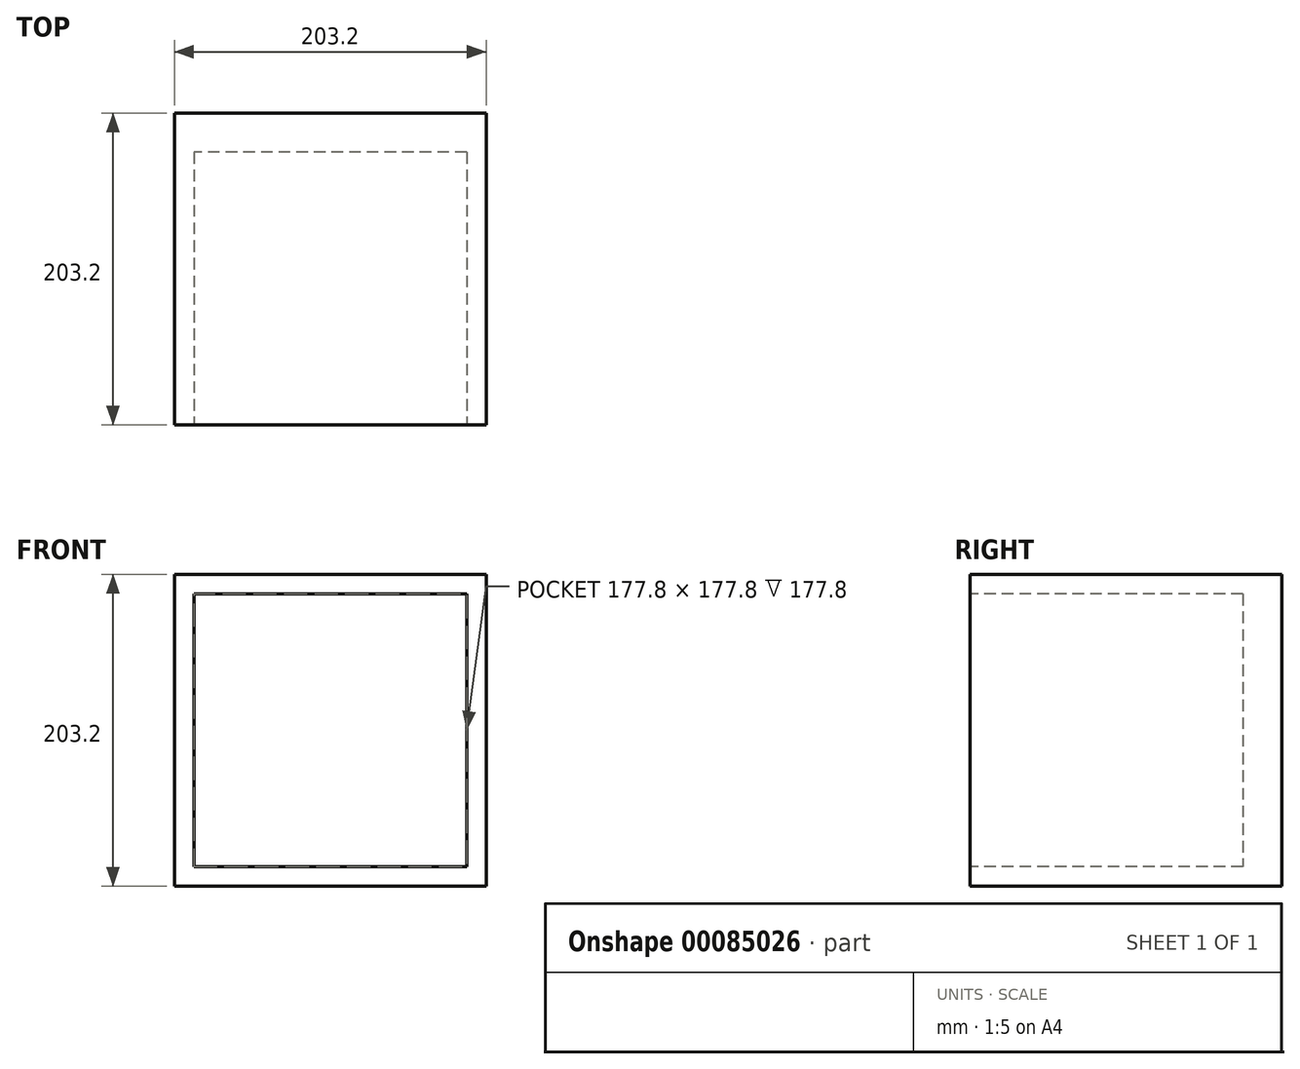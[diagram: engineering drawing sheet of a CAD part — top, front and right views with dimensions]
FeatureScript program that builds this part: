
annotation { "Feature Type Name" : "Feature", "Feature Type Description" : "" }
export const myFeature = defineFeature(function(context is Context, id is Id, definition is map)
    precondition{}
    {
        {
            var Q0;
            Q0=qCreatedBy(makeId("Front.planeOp"),FACE);
            var sketch = newSketch(context, id + "F0", { "sketchPlane" : qUnion([Q0])});
            skLineSegment(sketch, "E0.bottom", {"start": v(101.6, 101.6) * mm, "end": v(-101.6, 101.6) * mm});
            skLineSegment(sketch, "E0.top", {"start": v(101.6, -101.6) * mm, "end": v(-101.6, -101.6) * mm});
            skLineSegment(sketch, "E0.left", {"start": v(101.6, 101.6) * mm, "end": v(101.6, -101.6) * mm});
            skLineSegment(sketch, "E0.right", {"start": v(-101.6, 101.6) * mm, "end": v(-101.6, -101.6) * mm});
            skPoint(sketch, "E0.middle", {"position": v(0, 0) * mm});
            skSolve(sketch);
        }
        {
            var Q0;
            Q0 = qSketchRegion(id + "F0", true);
            extrude(context, id + "F1", {"entities" : qUnion([Q0]), "depth" : 203.2 * mm});
        }
        {
            var Q0;
            Q0=makeQuery(id+"F1.opExtrude","CAP_FACE",FACE,{"disambiguationData":[OSD([sQuery(id+"F0.wireOp",EDGE,"E0.bottom"),sQuery(id+"F0.wireOp",EDGE,"E0.top"),sQuery(id+"F0.wireOp",EDGE,"E0.left"),sQuery(id+"F0.wireOp",EDGE,"E0.right")])],"isStart":false});
            var sketch = newSketch(context, id + "F2", { "sketchPlane" : qUnion([Q0])});
            skLineSegment(sketch, "E1.bottom", {"start": v(88.9, 88.9) * mm, "end": v(-88.9, 88.9) * mm});
            skLineSegment(sketch, "E1.top", {"start": v(88.9, -88.9) * mm, "end": v(-88.9, -88.9) * mm});
            skLineSegment(sketch, "E1.left", {"start": v(88.9, 88.9) * mm, "end": v(88.9, -88.9) * mm});
            skLineSegment(sketch, "E1.right", {"start": v(-88.9, 88.9) * mm, "end": v(-88.9, -88.9) * mm});
            skPoint(sketch, "E1.middle", {"position": v(0, 0) * mm});
            skSolve(sketch);
        }
        {
            var Q0;
            Q0=makeQuery(id+"F2.imprint","IMPRINT",FACE,{"disambiguationData":[TD([[makeQuery(id+"F2.imprint","IMPRINT",EDGE,{"derivedFrom":sQuery(id+"F2.wireOp",EDGE,"E1.bottom")}),1.0]])]});
            extrude(context, id + "F3", {"entities" : qUnion([Q0]), "operationType" : NewBodyOperationType.REMOVE, "oppositeDirection" : true, "depth" : 177.8 * mm});
        }
    });
